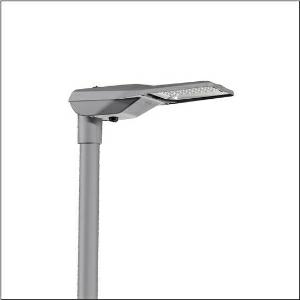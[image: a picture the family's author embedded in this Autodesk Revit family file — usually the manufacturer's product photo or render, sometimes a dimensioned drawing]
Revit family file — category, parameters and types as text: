
# Revit family: streetlight_sl_21_mini___pl52_5xe2h43t08hb_6adb
name_source: partatom
category: Lighting Fixtures
units: mm (PartAtom-declared; Revit-internal decimal feet)

## family parameters
Cut with Voids When Loaded = No
Host = Face
Light Source = No
Part Type = Normal
Room Calculation Point = No
Round Connector Dimension = Use Diameter
Shared = No

## types (1)
- --- (1 x LED, 9260 lm, 66 W, 4000K)
    Apparent Load = 66 VA
    CIE Flux Codes = 27 59 98 100 100
    Color Rendering = 70
    Color Temperature = 4000K
    Default Elevation = 1800 mm
    Description = Streetlight SL 21 mini, mast luminaire, primary light control with lens, of PMMA, primary optical cover: cover, of toughened safety glass, transparent, light distribution: PL52, light emission: direct distribution, primary light characteristic: asymmetric, installation type: side-entry, post-top, LED, High Power LED, rated luminous flux: 9.260lm, luminous efficacy: 140lm/W, light colour: 740, colour temperature: 4000K, control gear: D4i, control: overheat protection, constant luminous flux control, time-dependent luminous flux control, flexible luminous flux parameterisation, pre-setting: logarithmic dimming characteristic, mains connection: 220..240V, AC, 50/60Hz, start of lifetime: 66W, end of service life: 69W, reduction: 30W, luminaire housing, of diecast aluminium, powder-coated, SITECO metallic grey (DB 702S), corrosivity category C5 high according to DIN EN ISO 12944, please order mast flange separately, inclination adjustable: 0°, 5°, 10°, 15°, sealing non-destructively replaceable, multi-level sealing system, length: 628mm, width: 235mm, height: 110mm, mast flange for spigot size: 42mm (side-entry): 5XC10008XM4, 60/48mm (side-entry/post-top): 5XC10108XM2, 76/60mm (side-entry/post-top): 5XC10108XM1, mounting height: 4..8m, Smart Interface below and above, protection rating (complete): IP66, insulation class (complete): insulation class II (safety insulation), certification: CE, ENEC, ENEC+, VDE, impact resistance: IK10, permissible operating ambient temperature for outdoor applications: -40..+50°C, standard-compliant lighting for roads and squares, packaging unit: 1 piece

Light Distribution: PL52
    Height = 110 mm
    Lamp = 1 x LED
    Lamp Light Flux = 9260 lm
    Lamp Power = 66 W
    Lamp count = 1
    Length = 625 mm
    Luminous efficacy = 140 lm/W
    Manufacturer = Siteco
    ModVariant = No
    Model = 5XE2H43T08HB
    Number of Poles = 1
    OnlyDefault = Yes
    Power Factor = 1
    Product Name = Streetlight SL 21 mini | PL52
    Product group = mast luminaire | pylon top
    ProductGroupID = 6100
    Protection Class = Protection class II
    Protection Degree = IP 66
    RLX_Detail_Level = 1
    RLX_Emergency_Light_Flux = 0 lm
    RLX_Emergency_Type = 0
    RLX_Emergency_Type_DB = No
    RlxData = <blob elided: 35825 chars, md5=8e3a0d3c>
    Socket = socket
    Standby Power = 0 W
    System Light Flux = 9260 lm
    System Power = 66 W
    Type Comments = factory setting: luminous flux: 100 % | dim-lin: 254 | 670 mA
    Type Image = l_1003514.jpg
    URL = http://relux.com
    VarID = @adj_187411
    Voltage = 0 V
    Weight = 0.00 kg
    Width = 234 mm

## geometry (parser evidence)
native form markers: Blend x4, Sweep x11
no freeform markers — native parametric forms only
